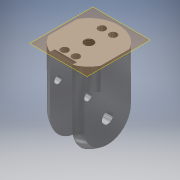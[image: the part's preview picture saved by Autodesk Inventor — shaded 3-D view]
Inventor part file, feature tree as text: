
AUTODESK INVENTOR PART (.ipt)
format: ipt  version: 2019 (Build 230136000, 136)  size: 167,936 bytes
history: native  units: in
note: dims shown in document units (in); Inventor stores cm internally (conversion verified against a paired STEP export)
features: reference x10, other x4, hole x2, sketch x2, projected_geometry x1
ambient origin geometry x8: Origin, YZ Plane, XZ Plane, XY Plane, X Axis, Y Axis, Z Axis, Center Point
bodies: Solid1 (feature_tree), Body (feature_tree)
feature tree (19):
  other  "plaszczyzna otwory"
  hole  "Otwór1"  [1 undecoded]
  hole  "Otwór2"  [1 undecoded]
  sketch  "Szkic1"
  reference  "Odniesienie1"
  projected_geometry  "Pętla rzutowana1"
  reference  "Odniesienie2"
  reference  "Odniesienie3"
  reference  "Odniesienie4"
  reference  "Odniesienie5"
  reference  "Odniesienie6"
  reference  "Odniesienie7"
  reference  "Odniesienie8"
  reference  "Odniesienie9"
  reference  "Odniesienie10"
  sketch  "Szkic2"
  other  "<userpath>\Downloads\reka\Finger all pieces assembled v10.iam"
  other  "Finger all pieces assembled v10.iam"
  other  "Base:1"
note: 2 required parameter values undecoded (feature->parameter linkage not recoverable at this tier; creation-order binding heuristic only, values carry confidence <= 0.55)
